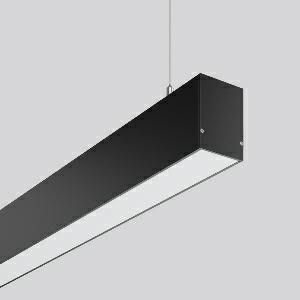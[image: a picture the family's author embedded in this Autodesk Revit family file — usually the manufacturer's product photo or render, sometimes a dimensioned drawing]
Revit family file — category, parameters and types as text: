
# Revit family: less_is_more_50_312315_003_0d84
name_source: partatom
category: Lighting Fixtures
units: mm (PartAtom-declared; Revit-internal decimal feet)

## family parameters
Cut with Voids When Loaded = No
Host = Face
Light Source = No
Part Type = Normal
Room Calculation Point = No
Round Connector Dimension = Use Diameter
Shared = No

## types (1)
- LESS IS MORE 50 (1 x LED Modul 830, 5400 lm, 3000)
    Apparent Load = 47 VA
    CIE Flux Codes = 48 79 95 100 100
    Color Rendering = 80
    Color Temperature = 3000
    Default Elevation = 1800 mm
    Description = Series: LESS IS MORE 50
Linear pendant luminaire for aesthetically sophisticated lighting. Housing: extruded aluminium profile, powder-coated. End cap aluminium powder-coated. Canopy made of aluminium, powder-coated. Diffuser made of non-yellowing plastic (PMMA), opal. Direct light emission. Suitable for pendant. 2-point steel cable suspension freely positionable and infinitely height-adjustable. Special lengths available on request. LED unit with integrated converter interchangeable and removable. Suitable for through-wiring. With sensors or as a safety luminaire on request. 
Colour: deep black, matt (RAL 9005)
Length: 1967 mm
Width: 57 mm
Height: 75 mm
Suspension length: 2000 mm
Lamp: LED
Socket: without socket
Colour temperature: 3000K
Colour rendering index (CRI): 80
System power: 47 W
Rated luminous flux: 5400 lm
Luminous efficiency: 115 lm/W
Control gear: Regulated power supply
Protection class: I
Type of protection: IP 20
    Height = 75 mm
    Lamp = 1 x LED Modul 830
    Lamp Light Flux = 5400 lm
    Lamp count = 1
    Length = 1967 mm
    Lifetime = 50000 h
    Luminous efficacy = 115 lm/W
    Manufacturer = RZB
    ModVariant = No
    Model = 312315.003
    Mounting Place = Ceiling
    Mounting Type = Pendant
    Number of Poles = 1
    OnlyDefault = Yes
    Power Factor = 1
    Product Name = LESS IS MORE 50
    Product group = Pendant LED linear luminaires
    ProductGroupID = 907
    Protection Class = Protection class I
    Protection Degree = IP 20
    RLX_Detail_Level = 1
    RLX_Emergency_Light_Flux = 0 lm
    RLX_Emergency_Type = 0
    RLX_Emergency_Type_DB = No
    RlxData = <blob elided: 28865 chars, md5=33473510>
    Socket = socket
    Standby Power = 0 W
    System Light Flux = 5400 lm
    System Power = 47 W
    Type Comments = Product without accessories
    Type Image = 312318.003.jpg
    URL = http://relux.com
    VarID = ---
    Voltage = 230 V
    Voltage Range = 220-240 V
    Weight = 0.00 kg
    Width = 57 mm

## geometry (parser evidence)
native form markers: Blend x4, Sweep x10
no freeform markers — native parametric forms only
